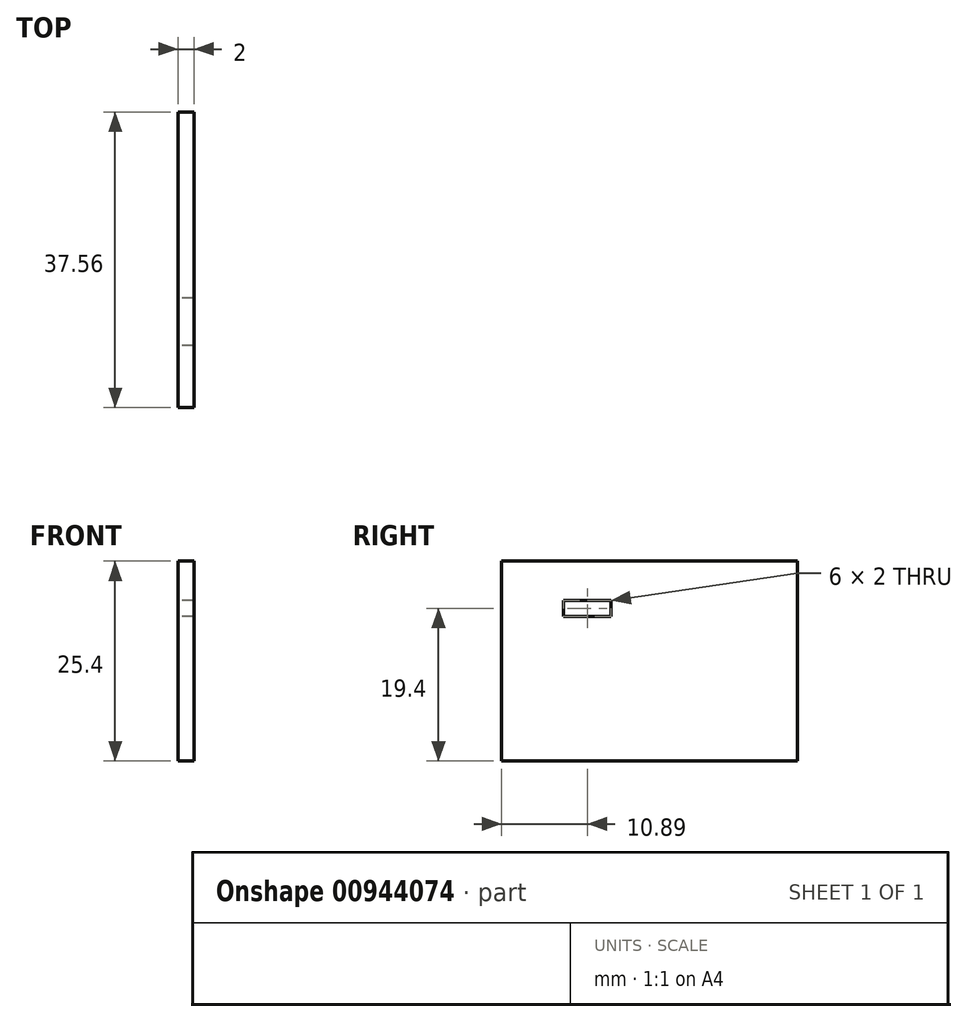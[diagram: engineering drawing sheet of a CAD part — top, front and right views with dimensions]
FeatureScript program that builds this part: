
annotation { "Feature Type Name" : "Feature", "Feature Type Description" : "" }
export const myFeature = defineFeature(function(context is Context, id is Id, definition is map)
    precondition{}
    {
        {
            var Q0;
            Q0=qCreatedBy(makeId("Right.planeOp"),FACE);
            var sketch = newSketch(context, id + "F0", { "sketchPlane" : qUnion([Q0])});
            skLineSegment(sketch, "E0.bottom", {"start": v(0, 25.4) * mm, "end": v(37.56, 25.4) * mm});
            skLineSegment(sketch, "E0.top", {"start": v(0, 0) * mm, "end": v(37.56, 0) * mm});
            skLineSegment(sketch, "E0.left", {"start": v(0, 25.4) * mm, "end": v(0, 0) * mm});
            skLineSegment(sketch, "E0.right", {"start": v(37.56, 25.4) * mm, "end": v(37.56, 0) * mm});
            skLineSegment(sketch, "E1.bottom", {"start": v(7.89, 20.4) * mm, "end": v(13.89, 20.4) * mm});
            skLineSegment(sketch, "E1.top", {"start": v(7.89, 18.4) * mm, "end": v(13.89, 18.4) * mm});
            skLineSegment(sketch, "E1.left", {"start": v(7.89, 20.4) * mm, "end": v(7.89, 18.4) * mm});
            skLineSegment(sketch, "E1.right", {"start": v(13.89, 20.4) * mm, "end": v(13.89, 18.4) * mm});
            skSolve(sketch);
        }
        {
            var Q0;
            Q0=qSketchRegion(id+"F0",true);
            extrude(context, id + "F1", {"entities" : qUnion([Q0]), "depth" : 2 * mm, "offsetDistance" : 25 * mm});
        }
    });
